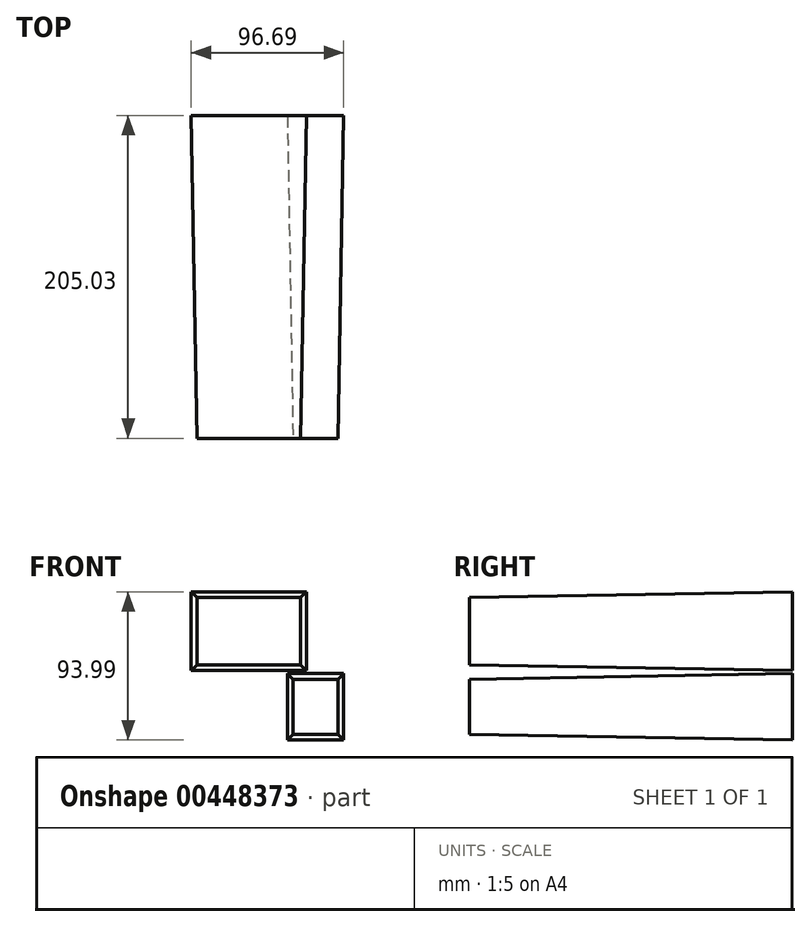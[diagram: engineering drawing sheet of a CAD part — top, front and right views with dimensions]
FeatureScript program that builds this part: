
annotation { "Feature Type Name" : "Feature", "Feature Type Description" : "" }
export const myFeature = defineFeature(function(context is Context, id is Id, definition is map)
    precondition{}
    {
        {
            var Q0;
            Q0=qCreatedBy(makeId("Front.planeOp"),FACE);
            var sketch = newSketch(context, id + "F0", { "sketchPlane" : qUnion([Q0])});
            skLineSegment(sketch, "E0.bottom", {"start": v(52.11, -53.21) * mm, "end": v(23.66, -53.21) * mm});
            skLineSegment(sketch, "E0.top", {"start": v(52.11, -18.3) * mm, "end": v(23.66, -18.3) * mm});
            skLineSegment(sketch, "E0.left", {"start": v(52.11, -53.21) * mm, "end": v(52.11, -18.3) * mm});
            skLineSegment(sketch, "E0.right", {"start": v(23.66, -53.21) * mm, "end": v(23.66, -18.3) * mm});
            skLineSegment(sketch, "E1.bottom", {"start": v(-37.42, 33.62) * mm, "end": v(28.5, 33.62) * mm});
            skLineSegment(sketch, "E1.top", {"start": v(-37.42, -9.12) * mm, "end": v(28.5, -9.12) * mm});
            skLineSegment(sketch, "E1.left", {"start": v(-37.42, 33.62) * mm, "end": v(-37.42, -9.12) * mm});
            skLineSegment(sketch, "E1.right", {"start": v(28.5, 33.62) * mm, "end": v(28.5, -9.12) * mm});
            skSolve(sketch);
        }
        {
            var Q0;
            Q0=makeQuery(id+"F0.imprint","IMPRINT",FACE,{"disambiguationData":[TD([[makeQuery(id+"F0.imprint","IMPRINT",EDGE,{"derivedFrom":sQuery(id+"F0.wireOp",EDGE,"E1.bottom")}),-1.0]])]});
            var Q1;
            Q1=makeQuery(id+"F0.imprint","IMPRINT",FACE,{"disambiguationData":[TD([[makeQuery(id+"F0.imprint","IMPRINT",EDGE,{"derivedFrom":sQuery(id+"F0.wireOp",EDGE,"E0.bottom")}),-1.0]])]});
            extrude(context, id + "F1", {"entities" : qUnion([Q0, Q1]), "oppositeDirection" : true, "depth" : 205.03 * mm, "hasDraft" : true, "draftAngle" : 1 * degree});
        }
    });
